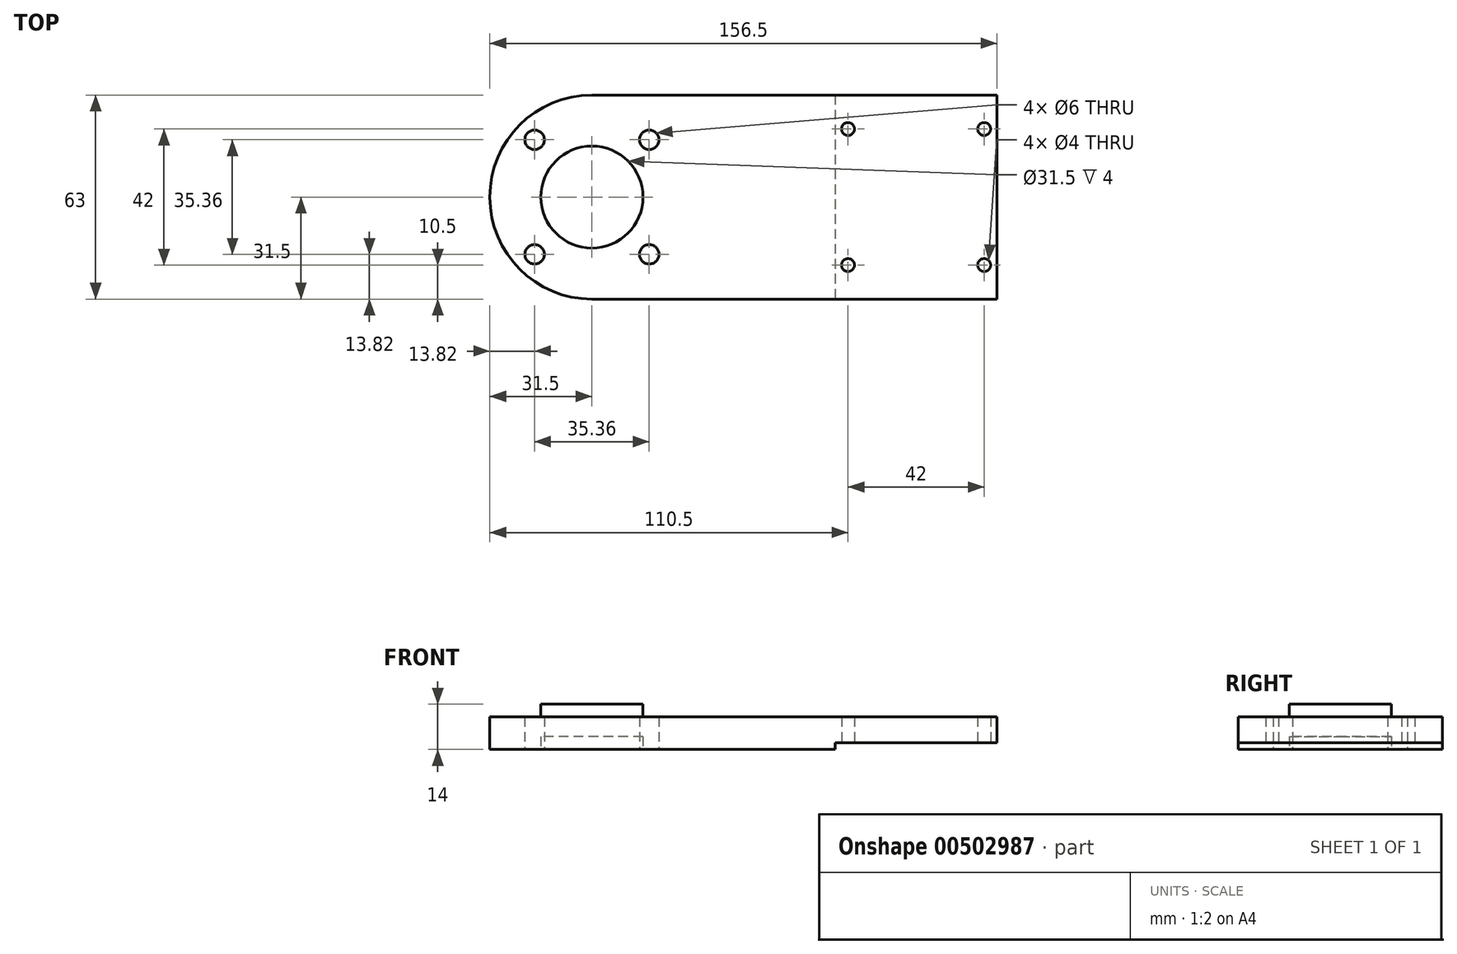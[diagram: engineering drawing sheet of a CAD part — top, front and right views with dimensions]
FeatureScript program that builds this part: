
annotation { "Feature Type Name" : "Feature", "Feature Type Description" : "" }
export const myFeature = defineFeature(function(context is Context, id is Id, definition is map)
    precondition{}
    {
        {
            var Q0;
            Q0=qCreatedBy(makeId("Top.planeOp"),FACE);
            var sketch = newSketch(context, id + "F0", { "sketchPlane" : qUnion([Q0])});
            skLineSegment(sketch, "E0.bottom", {"start": v(62.5, -31.5) * mm, "end": v(-62.5, -31.5) * mm});
            skLineSegment(sketch, "E0.top", {"start": v(62.5, 31.5) * mm, "end": v(-62.5, 31.5) * mm});
            skLineSegment(sketch, "E0.left", {"start": v(62.5, -31.5) * mm, "end": v(62.5, 31.5) * mm});
            skPoint(sketch, "E0.middle", {"position": v(0, 0) * mm});
            skArc(sketch, "E1", {"start": v(-62.5, 31.5) * mm, "mid": v(-94, 0) * mm, "end": v(-62.5, -31.5) * mm});
            skCircle(sketch, "E2", {"center": v(-80.18, -17.68) * mm, "radius": 3 * mm});
            skCircle(sketch, "E3", {"center": v(-44.82, -17.68) * mm, "radius": 3 * mm});
            skCircle(sketch, "E4", {"center": v(-44.82, 17.68) * mm, "radius": 3 * mm});
            skCircle(sketch, "E5", {"center": v(-80.18, 17.68) * mm, "radius": 3 * mm});
            skCircle(sketch, "E6", {"center": v(-62.5, 0) * mm, "radius": 15.75 * mm});
            skLineSegment(sketch, "E7", {"start": v(12.5, 31.5) * mm, "end": v(12.5, -31.5) * mm});
            skCircle(sketch, "E8", {"center": v(58.5, 21) * mm, "radius": 2 * mm});
            skCircle(sketch, "E9", {"center": v(16.5, 21) * mm, "radius": 2 * mm});
            skCircle(sketch, "E10", {"center": v(16.5, -21) * mm, "radius": 2 * mm});
            skCircle(sketch, "E11", {"center": v(58.5, -21) * mm, "radius": 2 * mm});
            skSolve(sketch);
        }
        {
            var Q0;
            {var subQ0=sQuery(id+"F0.wireOp",EDGE,"E1");Q0=makeQuery(id+"F0.imprint","IMPRINT",FACE,{"disambiguationData":[TD([[makeQuery(id+"F0.imprint","IMPRINT",EDGE,{"derivedFrom":subQ0}),1.0]])]});}
            extrude(context, id + "F1", {"entities" : qUnion([Q0]), "depth" : 10 * mm});
        }
        {
            var Q0;
            Q0=makeQuery(id+"F0.imprint","IMPRINT",FACE,{"disambiguationData":[TD([[makeQuery(id+"F0.imprint","IMPRINT",EDGE,{"derivedFrom":sQuery(id+"F0.wireOp",EDGE,"E6")}),1.0]])]});
            extrude(context, id + "F2", {"entities" : qUnion([Q0]), "operationType" : NewBodyOperationType.ADD, "depth" : 14 * mm});
        }
        {
            var Q0;
            {var subQ1=sQuery(id+"F0.wireOp",EDGE,"E0.left");Q0=makeQuery(id+"F0.imprint","IMPRINT",FACE,{"disambiguationData":[TD([[makeQuery(id+"F0.imprint","IMPRINT",EDGE,{"derivedFrom":subQ1}),1.0]])]});}
            extrude(context, id + "F3", {"entities" : qUnion([Q0]), "operationType" : NewBodyOperationType.ADD, "depth" : 10 * mm});
        }
        {
            var Q0;
            Q0=makeQuery(id+"F0.imprint","IMPRINT",FACE,{"disambiguationData":[TD([[makeQuery(id+"F0.imprint","IMPRINT",EDGE,{"derivedFrom":sQuery(id+"F0.wireOp",EDGE,"E6")}),1.0]])]});
            extrude(context, id + "F4", {"entities" : qUnion([Q0]), "operationType" : NewBodyOperationType.REMOVE, "depth" : 4 * mm});
        }
        {
            var Q0;
            {var subQ1=sQuery(id+"F0.wireOp",EDGE,"E0.left");Q0=makeQuery(id+"F0.imprint","IMPRINT",FACE,{"disambiguationData":[TD([[makeQuery(id+"F0.imprint","IMPRINT",EDGE,{"derivedFrom":subQ1}),1.0]])]});}
            extrude(context, id + "F5", {"entities" : qUnion([Q0]), "operationType" : NewBodyOperationType.REMOVE, "depth" : 2 * mm});
        }
    });
